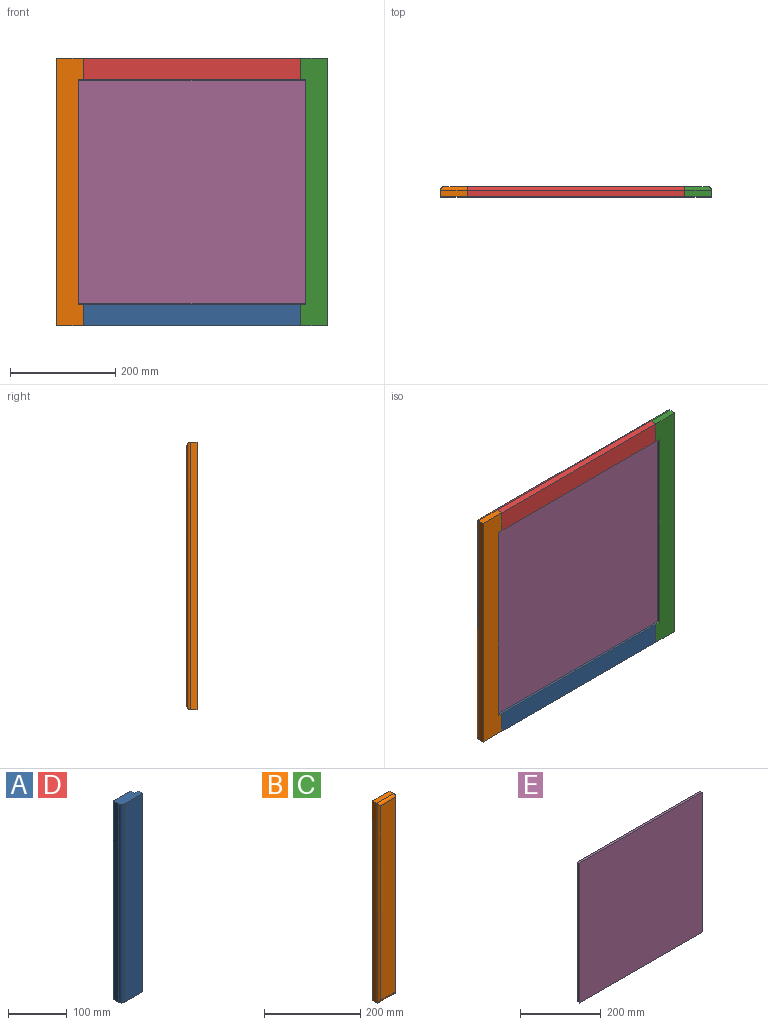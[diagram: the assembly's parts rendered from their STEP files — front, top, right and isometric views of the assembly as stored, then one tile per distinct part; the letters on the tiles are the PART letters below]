
ASSEMBLY  parts=5 mates=4
PART A: 9 faces, bbox 50.8x19.1x412.8 mm
  f0: plane 50.8x19.05mm, normal (0,0,1), area 868.4mm2, adj f2,f3,f4,f5,f6,f7,f8
  f1: plane 50.8x19.05mm, normal (0,0,-1), area 868.4mm2, adj f2,f3,f4,f5,f6,f7,f8
  f2: plane 412.75x12.7mm, normal (-1,0,0), area 5241.9mm2, adj f0,f1,f5,f6
  f3: plane 412.75x44.45mm, normal (0,-1,0), area 18346.7mm2, adj f0,f1,f4,f6
  f4: plane 412.75x9.53mm, normal (1,0,0), area 3931.4mm2, adj f0,f1,f3,f7
  f5: plane 412.75x41.28mm, normal (0,1,0), area 17036.3mm2, adj f0,f1,f2,f8
  f6: cylinder r=6.35mm len=412.75mm, axis (0,0,1), area 4117mm2, adj f0,f1,f2,f3
  f7: plane 412.75x9.53mm, normal (0,1,0), area 3931.4mm2, adj f0,f1,f4,f8
  f8: plane 412.75x9.53mm, normal (1,0,0), area 3931.4mm2, adj f0,f1,f5,f7
PART B: 13 faces, bbox 50.8x19.1x508 mm
  f0: plane 508x19.05mm, normal (1,0,0), area 5607.7mm2, adj f1,f3,f4,f5,f6,f7,f9,f10
  f1: plane 508x50.8mm, normal (0,1,0), area 21754mm2, adj f0,f2,f4,f5,f9,f10,f11
  f2: plane 508x12.7mm, normal (-1,0,0), area 6451.6mm2, adj f1,f4,f5,f8
  f3: plane 495.3x44.45mm, normal (0,-1,0), area 22016.1mm2, adj f0,f6,f7,f8
  f4: plane 50.8x12.7mm, normal (0,0,1), area 645.2mm2, adj f0,f1,f2,f6
  f5: plane 50.8x12.7mm, normal (0,0,-1), area 645.2mm2, adj f0,f1,f2,f7
  f6: cylinder r=6.35mm len=50.8mm, axis (-1,0,0), area 483.7mm2, adj f0,f3,f4,f8
  f7: cylinder r=6.35mm len=50.8mm, axis (1,0,0), area 483.7mm2, adj f0,f3,f5,f8
  f8: cylinder r=6.35mm len=508mm, axis (0,0,1), area 5021mm2, adj f2,f3,f6,f7
  f9: plane 9.53x9.53mm, normal (0,0,1), area 90.7mm2, adj f0,f1,f11,f12
  f10: plane 9.53x9.53mm, normal (0,0,-1), area 90.7mm2, adj f0,f1,f11,f12
  f11: plane 425.45x9.53mm, normal (1,0,0), area 4052.4mm2, adj f1,f9,f10,f12
  f12: plane 425.45x9.53mm, normal (0,1,0), area 4052.4mm2, adj f0,f9,f10,f11
PART C: same geometry as B
PART D: same geometry as A
PART E: 6 faces, bbox 430.2x6.4x423.9 mm
  f0: plane 423.86x6.35mm, normal (-1,0,0), area 2691.5mm2, adj f1,f3,f4,f5
  f1: plane 430.21x6.35mm, normal (0,0,-1), area 2731.8mm2, adj f0,f2,f4,f5
  f2: plane 423.86x6.35mm, normal (1,0,0), area 2691.5mm2, adj f1,f3,f4,f5
  f3: plane 430.21x6.35mm, normal (0,0,1), area 2731.8mm2, adj f0,f2,f4,f5
  f4: plane 430.21x423.86mm, normal (0,-1,0), area 182350.9mm2, adj f0,f1,f2,f3
  f5: plane 430.21x423.86mm, normal (0,1,0), area 182350.9mm2, adj f0,f1,f2,f3
PLACE A rot(axis=(-0.71,0,-0.71),180deg) t=(-434.98,0,-254)mm
PLACE B rot(axis=(-1,0,0),180deg) t=(-485.78,0,254)mm
PLACE C rot(axis=(0,0,1),180deg) t=(28.58,0,-254)mm
PLACE D rot(axis=(-0.71,0,0.71),180deg) t=(-22.22,0,254)mm
PLACE E rot(axis=(0,0,1),180deg) t=(-13.49,-15.88,-211.93)mm
MATE fastened C.f4 <-> D.f2  axis (0,0,1) through (-22.22,-12.7,254)mm
MATE fastened D.f0 <-> B.f0  axis (-1,0,0) through (-434.98,-19.05,254)mm
MATE fastened B.f0 <-> A.f1  axis (1,0,0) through (-434.98,-19.05,-254)mm
MATE fastened E.f4 <-> C.f12  axis (0,1,0) through (-13.49,-9.53,211.93)mm
